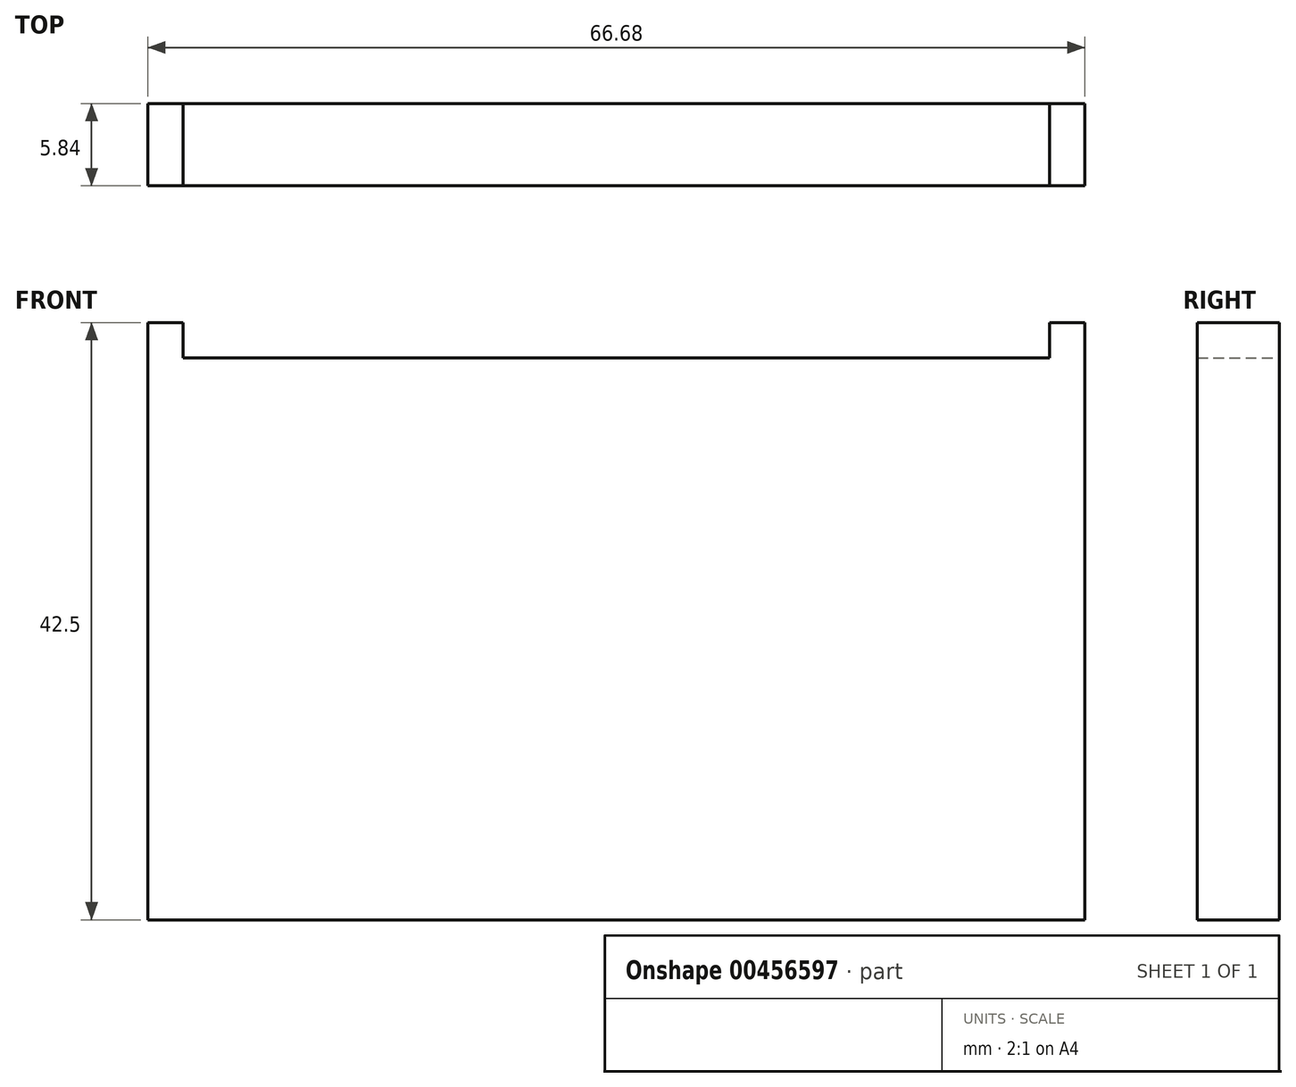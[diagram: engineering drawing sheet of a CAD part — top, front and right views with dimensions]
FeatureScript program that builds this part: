
annotation { "Feature Type Name" : "Feature", "Feature Type Description" : "" }
export const myFeature = defineFeature(function(context is Context, id is Id, definition is map)
    precondition{}
    {
        {
            var Q0;
            Q0=qCreatedBy(makeId("Front.planeOp"),FACE);
            var sketch = newSketch(context, id + "F0", { "sketchPlane" : qUnion([Q0])});
            skLineSegment(sketch, "E0.bottom", {"start": v(33.34, 21.25) * mm, "end": v(30.84, 21.25) * mm});
            skLineSegment(sketch, "E0.top", {"start": v(33.34, -21.25) * mm, "end": v(-33.34, -21.25) * mm});
            skLineSegment(sketch, "E0.left", {"start": v(33.34, 21.25) * mm, "end": v(33.34, -21.25) * mm});
            skLineSegment(sketch, "E0.right", {"start": v(-33.34, 21.25) * mm, "end": v(-33.34, -21.25) * mm});
            skPoint(sketch, "E0.middle", {"position": v(0, 0) * mm});
            skLineSegment(sketch, "E1.top", {"start": v(30.84, 18.75) * mm, "end": v(-30.84, 18.75) * mm});
            skLineSegment(sketch, "E1.left", {"start": v(30.84, 21.25) * mm, "end": v(30.84, 18.75) * mm});
            skLineSegment(sketch, "E1.right", {"start": v(-30.84, 21.25) * mm, "end": v(-30.84, 18.75) * mm});
            skPoint(sketch, "E1.middle", {"position": v(0, 21.25) * mm});
            skLineSegment(sketch, "E2.trimOffspring", {"start": v(-30.84, 21.25) * mm, "end": v(-33.34, 21.25) * mm});
            skPoint(sketch, "E3.orphan", {"position": v(-30.84, 23.75) * mm});
            skPoint(sketch, "E4.orphan", {"position": v(30.84, 23.75) * mm});
            skSolve(sketch);
        }
        {
            var Q0;
            Q0=qSketchRegion(id+"F0",true);
            extrude(context, id + "F1", {"entities" : qUnion([Q0]), "depth" : 5.84 * mm});
        }
    });
